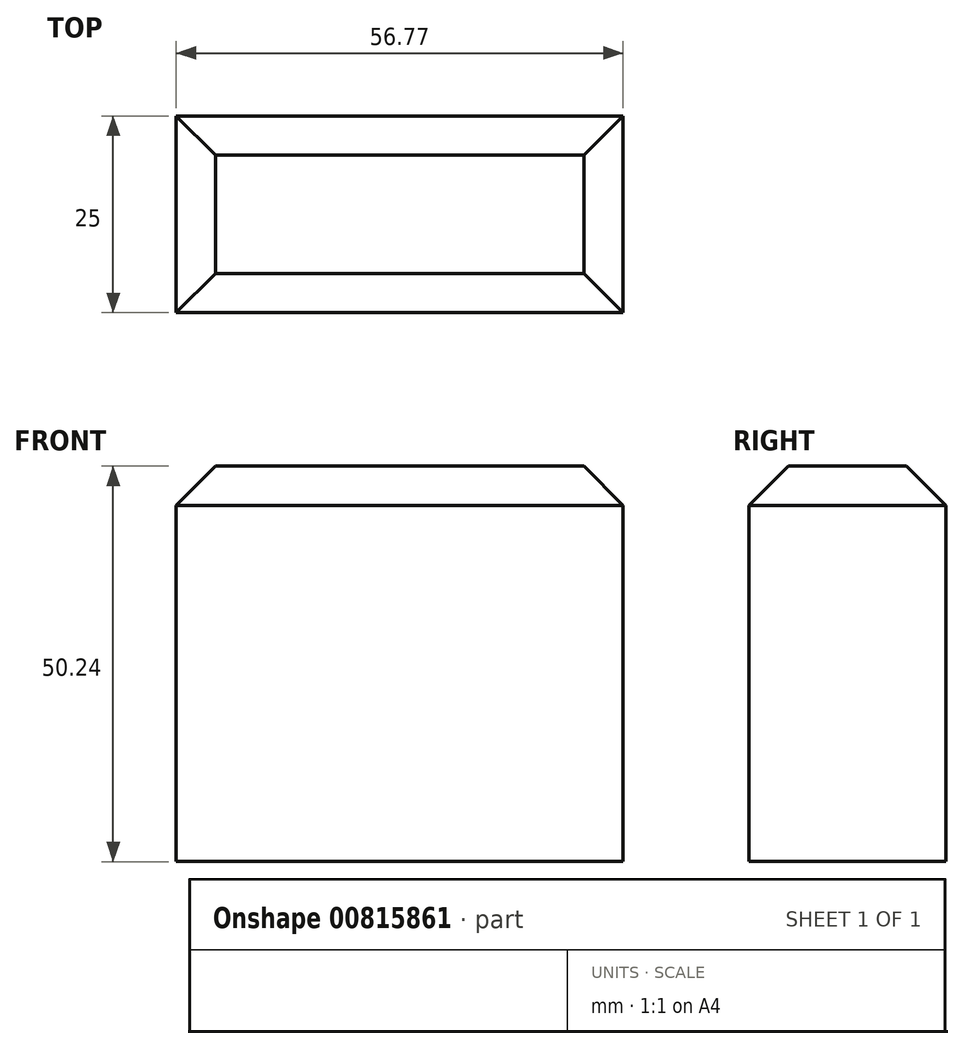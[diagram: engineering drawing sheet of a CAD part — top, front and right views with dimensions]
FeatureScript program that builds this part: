
annotation { "Feature Type Name" : "Feature", "Feature Type Description" : "" }
export const myFeature = defineFeature(function(context is Context, id is Id, definition is map)
    precondition{}
    {
        {
            var Q0;
            Q0=qCreatedBy(makeId("Front.planeOp"),FACE);
            var sketch = newSketch(context, id + "F0", { "sketchPlane" : qUnion([Q0])});
            skLineSegment(sketch, "E0.bottom", {"start": v(-134.14, 29.39) * mm, "end": v(-77.37, 29.39) * mm});
            skLineSegment(sketch, "E0.top", {"start": v(-134.14, -20.85) * mm, "end": v(-77.37, -20.85) * mm});
            skLineSegment(sketch, "E0.left", {"start": v(-134.14, 29.39) * mm, "end": v(-134.14, -20.85) * mm});
            skLineSegment(sketch, "E0.right", {"start": v(-77.37, 29.39) * mm, "end": v(-77.37, -20.85) * mm});
            skSolve(sketch);
        }
        {
            var Q0;
            Q0 = qSketchRegion(id + "F0", true);
            extrude(context, id + "F1", {"entities" : qUnion([Q0]), "depth" : 25 * mm, "offsetDistance" : 25 * mm});
        }
        {
            var Q0;
            Q0=makeQuery(id+"F1.opExtrude","SWEPT_FACE",FACE,{"disambiguationData":[OSD([sQuery(id+"F0.wireOp",EDGE,"E0.bottom")])]});
            chamfer(context, id + "F2", {"entities" : qUnion([Q0]), "width" : 5 * mm, "tangentPropagation" : true});
        }
    });
